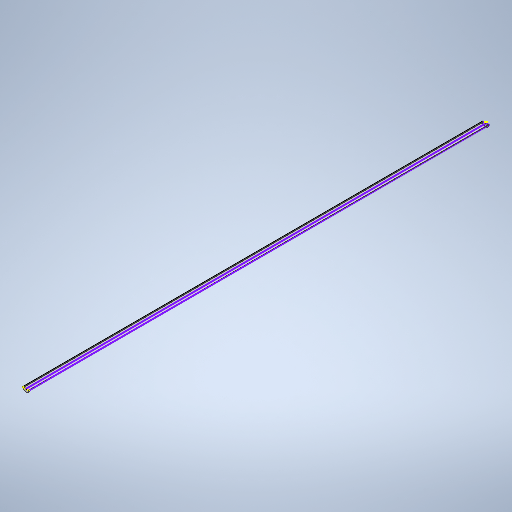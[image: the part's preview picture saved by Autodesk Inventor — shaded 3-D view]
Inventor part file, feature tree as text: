
AUTODESK INVENTOR PART (.ipt)
format: ipt  version: 2025.3 (Build 293356000, 356)  size: 260,608 bytes
history: native  units: mm
features: sketch x4, extrude x3, other x1
ambient origin geometry x8: Origin, YZ Plane, XZ Plane, XY Plane, X Axis, Y Axis, Z Axis, Center Point
bodies: Body1 (feature_tree)
feature tree (8):
  other  "Sólido1"
  extrude  "Extrusión1"  Depth=68.0mm
  extrude  "Extrusión2"  Depth=6100.0mm
  extrude  "Extrusión3"  Depth=5.0mm TaperAngle=0.0deg
  sketch  "Boceto4"
  sketch  "Boceto1"  dims[d0=76.2mm d1=68.0mm]
  sketch  "Boceto2"  dims[d2=6100.0mm d3=0.0mm d4=79.0mm]
  sketch  "Boceto3"  dims[d5=5.0mm d6=5.0mm d7=0.0mm d8=0.0mm d9=5.0mm d10=5.0mm d11=0.0mm d12=0.0mm]
